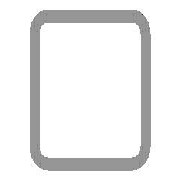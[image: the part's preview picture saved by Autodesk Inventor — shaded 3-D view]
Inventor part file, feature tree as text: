
AUTODESK INVENTOR PART (.ipt)
format: ipt  version: 2025.3 (Build 293356030, 356C)  size: 143,872 bytes
history: native  units: mm (DEFAULTED — no unit token found)
features: other x4, plane x2, split x1, sketch x1
ambient origin geometry x8: Origin, YZ Plane, XZ Plane, XY Plane, X Axis, Y Axis, Z Axis, Center Point
bodies: Solid1 (feature_tree), Body (feature_tree)
feature tree (8):
  parser-record x1  (decoder bookkeeping rows leaked as tree rows — omitted from the tree; the rows remain in map.json)
  other  "Driven Length"
  other  "Start Plane"
  other  "End Plane"
  plane  "Work Plane4"
  split  "Split1"
  sketch  "Sketch3"  dims[d3=2559.340203mm d4=0.0mm d7=6.0mm d9=80.0mm d11=80.0mm d12=3.0mm d13=160.659797mm d14=2720.0mm d15=40.0mm d16=40.0mm d17=90.0deg d18=2559.340203mm]
  plane  "Work Plane3"
